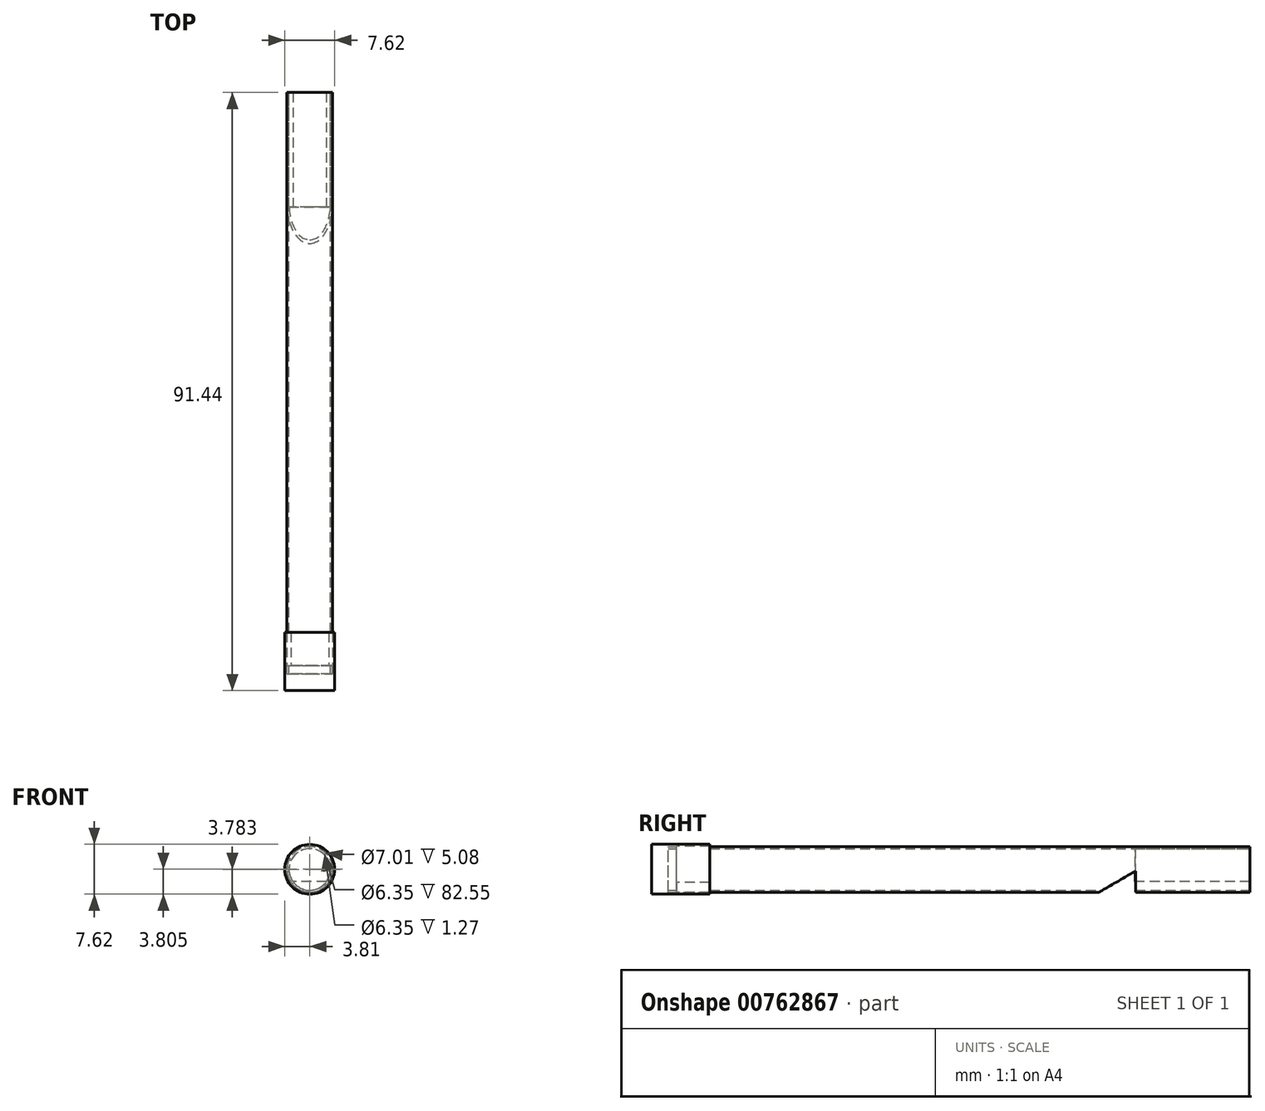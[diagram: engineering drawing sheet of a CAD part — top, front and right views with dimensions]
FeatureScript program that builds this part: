
annotation { "Feature Type Name" : "Feature", "Feature Type Description" : "" }
export const myFeature = defineFeature(function(context is Context, id is Id, definition is map)
    precondition{}
    {
        {
            var Q0;
            Q0=qCreatedBy(makeId("Front.planeOp"),FACE);
            var sketch = newSketch(context, id + "F0", { "sketchPlane" : qUnion([Q0])});
            skCircle(sketch, "E0", {"center": v(0, 3.5) * mm, "radius": 3.5 * mm});
            skCircle(sketch, "E1", {"center": v(0, 3.5) * mm, "radius": 3.18 * mm});
            skSolve(sketch);
        }
        {
            var Q0;
            Q0=qCreatedBy(makeId("Right.planeOp"),FACE);
            var sketch = newSketch(context, id + "F1", { "sketchPlane" : qUnion([Q0])});
            skLineSegment(sketch, "E2", {"start": v(-17.48, 0) * mm, "end": v(-17.48, -3.24) * mm});
            skLineSegment(sketch, "E3", {"start": v(-17.48, -3.24) * mm, "end": v(-23.08, 0) * mm});
            skLineSegment(sketch, "E4", {"start": v(-23.08, 0) * mm, "end": v(-17.48, 0) * mm});
            skLineSegment(sketch, "E5.MirrorCS", {"start": v(-17.48, 3.24) * mm, "end": v(-23.08, 0) * mm});
            skLineSegment(sketch, "E6.MirrorCS", {"start": v(-17.48, 0) * mm, "end": v(-17.48, 3.24) * mm});
            skSolve(sketch);
        }
        {
            var Q0;
            Q0 = qSketchRegion(id + "F0", true);
            extrude(context, id + "F2", {"entities" : qUnion([Q0]), "depth" : 88.9 * mm, "offsetDistance" : 25.4 * mm});
        }
        {
            var Q0;
            Q0 = qSketchRegion(id + "F0", true);
            extrude(context, id + "F3", {"entities" : qUnion([Q0]), "operationType" : NewBodyOperationType.ADD, "depth" : 25.4 * mm, "offsetDistance" : 25.4 * mm});
        }
        {
            var Q0;
            Q0 = qSketchRegion(id + "F1", true);
            extrude(context, id + "F4", {"entities" : qUnion([Q0]), "operationType" : NewBodyOperationType.REMOVE, "oppositeDirection" : true, "depth" : 25.4 * mm, "offsetDistance" : 25.4 * mm, "hasSecondDirection" : true, "secondDirectionOppositeDirection" : true, "secondDirectionDepth" : -25.4 * mm});
        }
        {
            var Q0;
            Q0=qCreatedBy(makeId("Front.planeOp"),FACE);
            var sketch = newSketch(context, id + "F5", { "sketchPlane" : qUnion([Q0])});
            skCircle(sketch, "E7", {"center": v(0, 3.5) * mm, "radius": 3.17 * mm});
            skSolve(sketch);
        }
        {
            var Q0;
            Q0 = qSketchRegion(id + "F5", true);
            extrude(context, id + "F6", {"entities" : qUnion([Q0]), "depth" : 17.53 * mm, "offsetDistance" : 25.4 * mm});
        }
        {
            var Q0;
            Q0=makeQuery(id+"F6.opExtrude","CAP_FACE",FACE,{"disambiguationData":[OSD([sQuery(id+"F5.wireOp",EDGE,"E7")])],"isStart":false});
            var sketch = newSketch(context, id + "F7", { "sketchPlane" : qUnion([Q0])});
            skLineSegment(sketch, "E8", {"start": v(2.54, 1.62) * mm, "end": v(-2.54, 1.62) * mm});
            skArc(sketch, "E9", {"start": v(-2.54, 1.62) * mm, "mid": v(0, 0.34) * mm, "end": v(2.54, 1.62) * mm});
            skSolve(sketch);
        }
        {
            var Q0;
            Q0 = qSketchRegion(id + "F7", true);
            extrude(context, id + "F8", {"entities" : qUnion([Q0]), "operationType" : NewBodyOperationType.REMOVE, "oppositeDirection" : true, "depth" : 17.78 * mm, "offsetDistance" : 25.4 * mm});
        }
        {
            var Q0;
            Q0=qCreatedBy(makeId("Front.planeOp"),FACE);
            cPlane(context, id + "F9", {"entities" : qUnion([Q0]), "cplaneType" : CPlaneType.OFFSET, "offset" : 88.9 * mm, "width" : 152.4 * mm, "height" : 152.4 * mm});
        }
        {
            var Q0;
            Q0=qCreatedBy(id+"F9.planeOp",FACE);
            var sketch = newSketch(context, id + "F10", { "sketchPlane" : qUnion([Q0])});
            skCircle(sketch, "E10", {"center": v(0, 3.52) * mm, "radius": 3.8 * mm});
            skSolve(sketch);
        }
        {
            var Q0;
            Q0 = qSketchRegion(id + "F10", true);
            extrude(context, id + "F11", {"entities" : qUnion([Q0]), "depth" : 2.54 * mm, "offsetDistance" : 25.4 * mm, "hasSecondDirection" : true, "secondDirectionOppositeDirection" : true, "secondDirectionDepth" : 6.35 * mm});
        }
        {
            var Q0;
            Q0=qCreatedBy(id+"F9.planeOp",FACE);
            var sketch = newSketch(context, id + "F12", { "sketchPlane" : qUnion([Q0])});
            skCircle(sketch, "E11", {"center": v(0, 3.52) * mm, "radius": 3.5 * mm});
            skSolve(sketch);
        }
        {
            var Q0;
            Q0 = qSketchRegion(id + "F12", true);
            extrude(context, id + "F13", {"entities" : qUnion([Q0]), "operationType" : NewBodyOperationType.REMOVE, "oppositeDirection" : true, "depth" : 6.35 * mm, "offsetDistance" : 25.4 * mm, "hasSecondDirection" : true, "secondDirectionOppositeDirection" : true, "secondDirectionDepth" : 1.27 * mm});
        }
    });
